# Revit family: 3080091 Feilo Sylvania Lighting Fixtures INVERTO DIRECT WW 1-10V SILVER
name_source: partatom
category: Lighting Fixtures
revit_build: Autodesk Revit 2017 (Build: 20190507_1515(x64)
units: mm (PartAtom-declared; Revit-internal decimal feet)

## family parameters
Cut with Voids When Loaded = No
Host = Face
Light Source = Yes
Part Type = Normal
Room Calculation Point = No
Round Connector Dimension = Use Diameter
Shared = No

## types (1)
- 3080091 INVERTO DIRECT WW 1-10V SILVER
    Apparent Load = 16 VA
    Assembly Code = D5020200
    AssetType = Fixed
    Calculate Coefficient of Utilization = No
    Color Filter = 16777215
    Cost = 0 $
    Default Elevation = 1219 mm
    Description = Surface Wall mounted luminaire, wire to base with pluggable connection for easy installation,  suitable for looping, switchable driver, silver coloured aluminium housing, 1,617lm or 2,045lm, 16W or 19W, 102lm/W or 107lm/W, 3000K, 350mA or 450mA , CRI:80,  40° beam Angle, 1-10V dimmable, IP65, IK02, 50,000hrs (L70),  23.00x19.4x11.5mm.
    Dimming Lamp Color Temperature Shift = <None>
    DimmingControlOptions = Dimmable
    DocumentationLiterature = http://www.sylvania-lighting.com
    DurationUnit = hours
    ElectricShockClassification = Class I
    Emit Shape Visible in Rendering = No
    Emit from Rectangle Length = 90 mm  [stored 0.295276 ft]
    Emit from Rectangle Width = 90 mm  [stored 0.295276 ft]
    ExpectedLife = 50000
    Housing material = Aluminum 1100-H14
    IfcExportAs = IfcLightFixtureType
    IfcExportType = IfcLightFixtureType
    ImpactProtectionIndex = IK07
    IngressProtection = IP65
    InputNominalFrequency = 50/60 Hz
    InputVoltage = 220-240V~
    Keynote = 16500
    Lamp = LED
    LampColourRenderingIndex = 80
    LampColourTemperature = 3000 K
    LampNominalLuminous = 1566 / 1980 lm
    LampsType = LED
    LightOutputRatio = 100
    LuminousEfficacy = 98 lm/W
    Manufacturer = Feilo Sylvania
    ManufacturerName = Feilo Sylvania
    Material = aluminium housing, glass diffuser
    Model = INVERTO DIRECT WW 1-10V SILVER
    ModelNumber = 3080091
    ModelReference = INVERTO DIRECT WW 1-10V SILVER
    Name = INVERTO DIRECT WW 1-10V SILVER
    NominalDepth = 110 mm  [stored 0.360892 ft]
    NominalHeight = 110 mm  [stored 0.360892 ft]
    NominalLength = 162 mm
    Photometric Web File = 3080091.ies
    PowerConsumption = 16 W
    PowerFactor = 0
    Tilt Angle = -90.00°
    Type Image = <None>
    TypeName = INVERTO DIRECT WW 1-10V SILVER
    URL = http://www.sylvania-lighting.com
    Voltage = 230 V
    Weight = 1.461 kg

note: [stored X ft] marks values corroborated as IEEE doubles in the binary element streams (Revit-internal decimal feet)

## geometry (parser evidence)
native form markers: Sweep x3
no freeform markers — native parametric forms only
